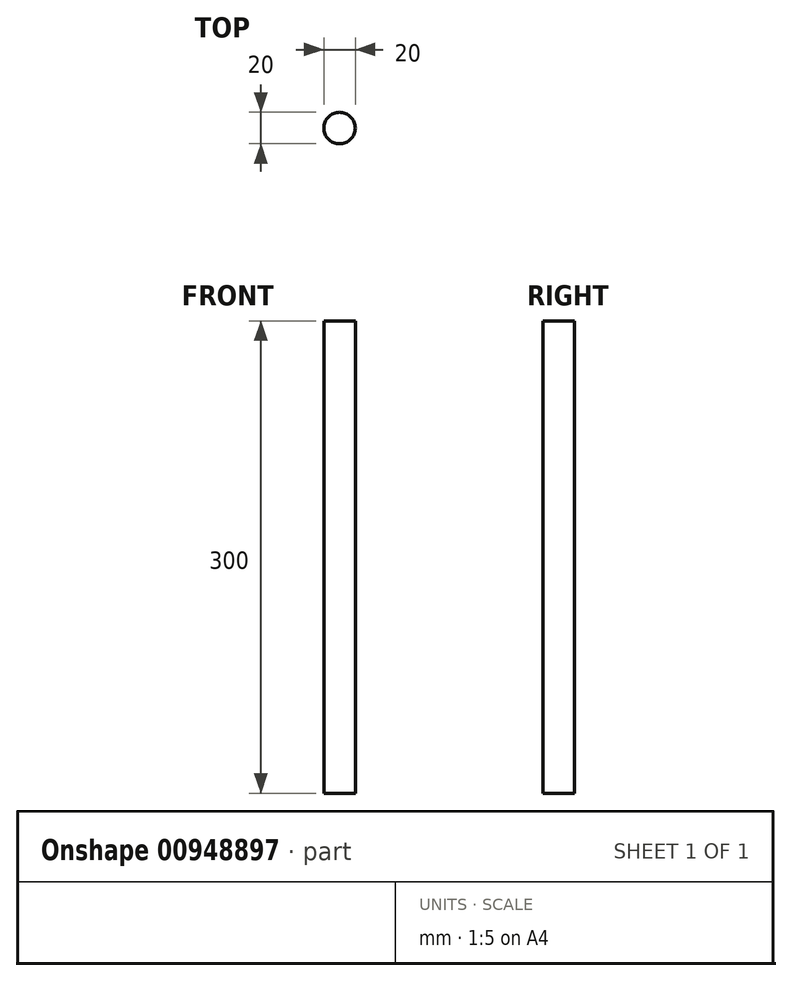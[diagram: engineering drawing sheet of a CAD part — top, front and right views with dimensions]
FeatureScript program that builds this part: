
annotation { "Feature Type Name" : "Feature", "Feature Type Description" : "" }
export const myFeature = defineFeature(function(context is Context, id is Id, definition is map)
    precondition{}
    {
        {
            var Q0;
            Q0=qCreatedBy(makeId("Top.planeOp"),FACE);
            var sketch = newSketch(context, id + "F0", { "sketchPlane" : qUnion([Q0])});
            skCircle(sketch, "E0", {"center": v(0, 0) * mm, "radius": 10 * mm});
            skSolve(sketch);
        }
        {
            var Q0;
            Q0=makeQuery(id+"F0.imprint","IMPRINT",FACE,{"disambiguationData":[TD([[makeQuery(id+"F0.imprint","IMPRINT",EDGE,{"derivedFrom":sQuery(id+"F0.wireOp",EDGE,"E0")}),1.0]])]});
            extrude(context, id + "F1", {"entities" : qUnion([Q0]), "depth" : 300 * mm, "offsetDistance" : 25 * mm});
        }
    });
